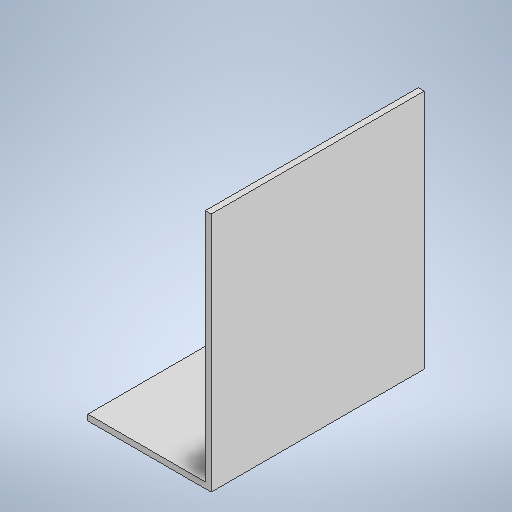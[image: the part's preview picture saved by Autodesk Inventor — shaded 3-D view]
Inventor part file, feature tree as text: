
AUTODESK INVENTOR PART (.ipt)
format: ipt  version: 2025.1 (Build 291241020, 241B)  size: 210,944 bytes
history: native  units: in
note: dims shown in document units (in); Inventor stores cm internally (conversion verified against a paired STEP export)
features: extrude x2, sketch x2
ambient origin geometry x8: Origin, YZ Plane, XZ Plane, XY Plane, X Axis, Y Axis, Z Axis, Center Point
bodies: Solid1 (feature_tree)
feature tree (4):
  extrude  "Extrusion1"  Depth=4.2in
  extrude  "Extrusion2"  Depth=0.2in
  sketch  "Sketch1"  dims[d0=7.25in d1=4.2in]
  sketch  "Sketch2"  dims[d2=0.2in d3=0.0in d4=0.2in d5=8.0in d6=0.0in]
